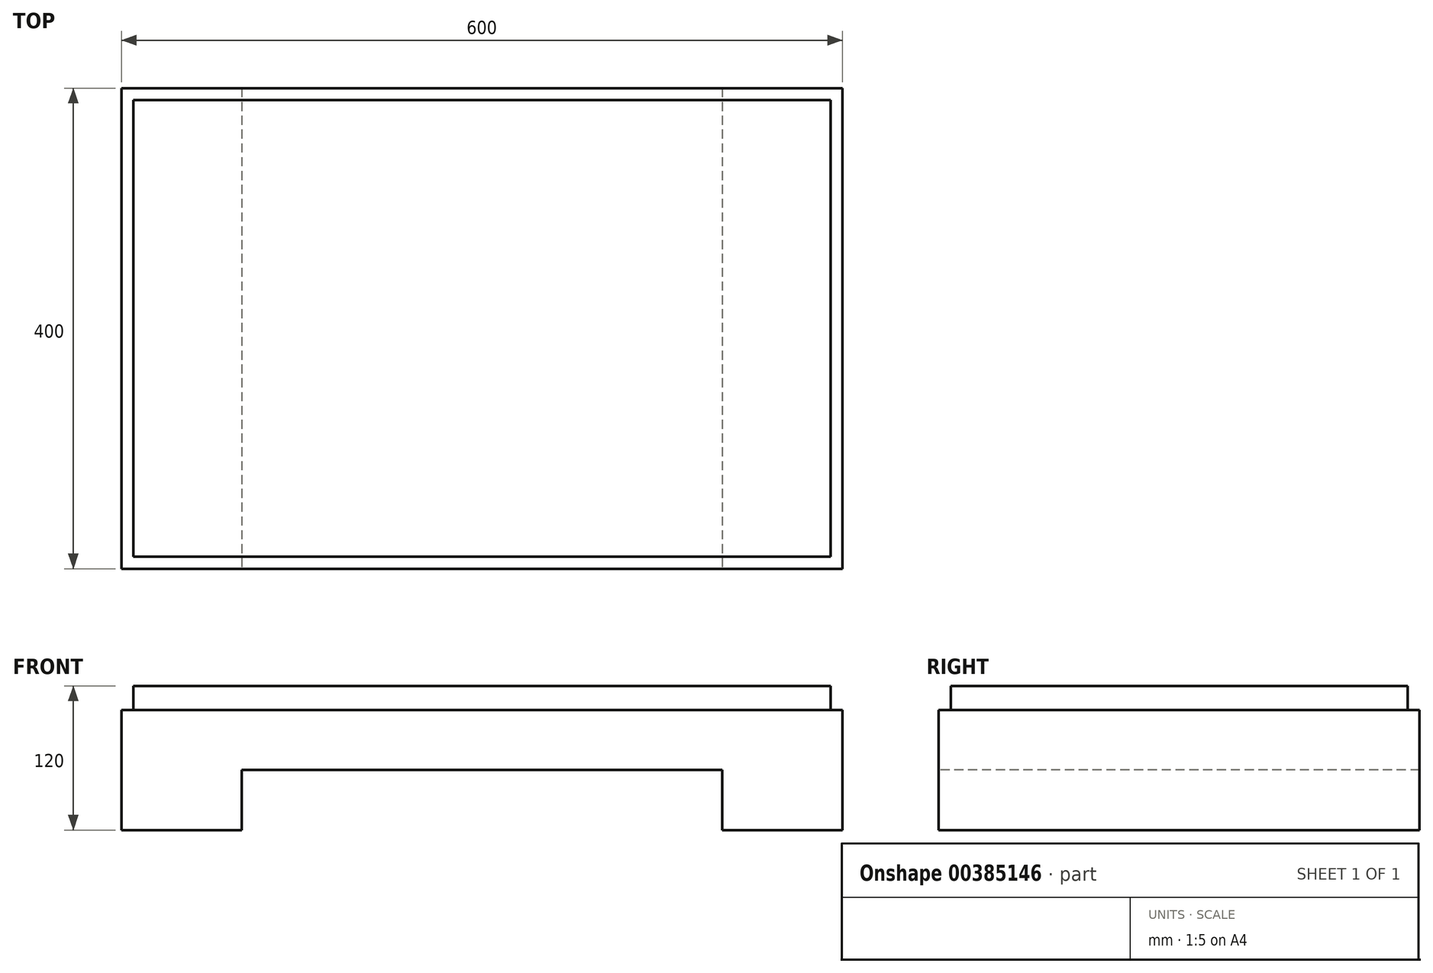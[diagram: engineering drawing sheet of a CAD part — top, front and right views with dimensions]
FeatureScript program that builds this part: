
annotation { "Feature Type Name" : "Feature", "Feature Type Description" : "" }
export const myFeature = defineFeature(function(context is Context, id is Id, definition is map)
    precondition{}
    {
        {
            var Q0;
            Q0=qCreatedBy(makeId("Top.planeOp"),FACE);
            var sketch = newSketch(context, id + "F0", { "sketchPlane" : qUnion([Q0])});
            skLineSegment(sketch, "E0.bottom", {"start": v(-300, 200) * mm, "end": v(300, 200) * mm});
            skLineSegment(sketch, "E0.top", {"start": v(-300, -200) * mm, "end": v(300, -200) * mm});
            skLineSegment(sketch, "E0.left", {"start": v(-300, 200) * mm, "end": v(-300, -200) * mm});
            skLineSegment(sketch, "E0.right", {"start": v(300, 200) * mm, "end": v(300, -200) * mm});
            skPoint(sketch, "E0.middle", {"position": v(0, 0) * mm});
            skSolve(sketch);
        }
        {
            var Q0;
            Q0=makeQuery(id+"F0.imprint","IMPRINT",FACE,{"disambiguationData":[TD([[makeQuery(id+"F0.imprint","IMPRINT",EDGE,{"derivedFrom":sQuery(id+"F0.wireOp",EDGE,"E0.bottom")}),-1.0]])]});
            extrude(context, id + "F1", {"entities" : qUnion([Q0]), "oppositeDirection" : true, "depth" : 100 * mm});
        }
        {
            var Q0;
            Q0=makeQuery(id+"F1.opExtrude","CAP_FACE",FACE,{"disambiguationData":[OSD([sQuery(id+"F0.wireOp",EDGE,"E0.bottom"),sQuery(id+"F0.wireOp",EDGE,"E0.top"),sQuery(id+"F0.wireOp",EDGE,"E0.left"),sQuery(id+"F0.wireOp",EDGE,"E0.right")])],"isStart":false});
            var sketch = newSketch(context, id + "F2", { "sketchPlane" : qUnion([Q0])});
            skLineSegment(sketch, "E1.bottom", {"start": v(-290, 190) * mm, "end": v(290, 190) * mm});
            skLineSegment(sketch, "E1.top", {"start": v(-290, -190) * mm, "end": v(290, -190) * mm});
            skLineSegment(sketch, "E1.left", {"start": v(-290, 190) * mm, "end": v(-290, -190) * mm});
            skLineSegment(sketch, "E1.right", {"start": v(290, 190) * mm, "end": v(290, -190) * mm});
            skPoint(sketch, "E1.middle", {"position": v(0, 0) * mm});
            skSolve(sketch);
        }
        {
            var Q0;
            Q0=makeQuery(id+"F2.imprint","IMPRINT",FACE,{"disambiguationData":[TD([[makeQuery(id+"F2.imprint","IMPRINT",EDGE,{"derivedFrom":sQuery(id+"F2.wireOp",EDGE,"E1.bottom")}),-1.0]])]});
            extrude(context, id + "F3", {"entities" : qUnion([Q0]), "operationType" : NewBodyOperationType.REMOVE, "oppositeDirection" : true, "depth" : 80 * mm});
        }
        {
            var Q0;
            Q0=makeQuery(id+"F1.opExtrude","SWEPT_FACE",FACE,{"disambiguationData":[OSD([sQuery(id+"F0.wireOp",EDGE,"E0.top")])]});
            var sketch = newSketch(context, id + "F4", { "sketchPlane" : qUnion([Q0])});
            skLineSegment(sketch, "E2", {"start": v(-200, -100) * mm, "end": v(-200, -50) * mm});
            skLineSegment(sketch, "E3", {"start": v(-200, -50) * mm, "end": v(200, -50) * mm});
            skPoint(sketch, "E3.endSnap0", {"position": v(300, -50) * mm});
            skLineSegment(sketch, "E4", {"start": v(200, -50) * mm, "end": v(200, -100) * mm});
            skSolve(sketch);
        }
        {
            var Q0;
            Q0 = qSketchRegion(id + "F4", true);
            var Q1;
            {var subQ0=sQuery(id+"F4.wireOp",EDGE,"E2");Q1=makeQuery(id+"F4.imprint","IMPRINT",FACE,{"disambiguationData":[TD([[makeQuery(id+"F4.imprint","IMPRINT",EDGE,{"derivedFrom":subQ0}),-1.0]])]});}
            extrude(context, id + "F5", {"entities" : qUnion([Q0, Q1]), "operationType" : NewBodyOperationType.REMOVE, "oppositeDirection" : true, "depth" : 25 * mm});
        }
        {
            var Q0;
            Q0=makeQuery(id+"F1.opExtrude","SWEPT_FACE",FACE,{"disambiguationData":[OSD([sQuery(id+"F0.wireOp",EDGE,"E0.bottom")])]});
            var sketch = newSketch(context, id + "F6", { "sketchPlane" : qUnion([Q0])});
            skLineSegment(sketch, "E5", {"start": v(-200, -100) * mm, "end": v(-200, -50) * mm});
            skLineSegment(sketch, "E6", {"start": v(-200, -50) * mm, "end": v(200, -50) * mm});
            skLineSegment(sketch, "E7", {"start": v(200, -50) * mm, "end": v(200, -100) * mm});
            skSolve(sketch);
        }
        {
            var Q0;
            Q0 = qSketchRegion(id + "F6", true);
            var Q1;
            {var subQ0=sQuery(id+"F6.wireOp",EDGE,"E5");Q1=makeQuery(id+"F6.imprint","IMPRINT",FACE,{"disambiguationData":[TD([[makeQuery(id+"F6.imprint","IMPRINT",EDGE,{"derivedFrom":subQ0}),-1.0]])]});}
            extrude(context, id + "F7", {"entities" : qUnion([Q0, Q1]), "operationType" : NewBodyOperationType.REMOVE, "oppositeDirection" : true, "depth" : 25 * mm});
        }
        {
            var Q0;
            Q0=makeQuery(id+"F1.opExtrude","CAP_FACE",FACE,{"disambiguationData":[OSD([sQuery(id+"F0.wireOp",EDGE,"E0.bottom"),sQuery(id+"F0.wireOp",EDGE,"E0.top"),sQuery(id+"F0.wireOp",EDGE,"E0.left"),sQuery(id+"F0.wireOp",EDGE,"E0.right")])],"isStart":true});
            var sketch = newSketch(context, id + "F8", { "sketchPlane" : qUnion([Q0])});
            skLineSegment(sketch, "E8.bottom", {"start": v(290, -190) * mm, "end": v(-290, -190) * mm});
            skLineSegment(sketch, "E8.top", {"start": v(290, 190) * mm, "end": v(-290, 190) * mm});
            skLineSegment(sketch, "E8.left", {"start": v(290, -190) * mm, "end": v(290, 190) * mm});
            skLineSegment(sketch, "E8.right", {"start": v(-290, -190) * mm, "end": v(-290, 190) * mm});
            skPoint(sketch, "E8.middle", {"position": v(0, 0) * mm});
            skSolve(sketch);
        }
        {
            var Q0;
            Q0=makeQuery(id+"F8.imprint","IMPRINT",FACE,{"disambiguationData":[TD([[makeQuery(id+"F8.imprint","IMPRINT",EDGE,{"derivedFrom":sQuery(id+"F8.wireOp",EDGE,"E8.bottom")}),-1.0]])]});
            extrude(context, id + "F9", {"entities" : qUnion([Q0]), "operationType" : NewBodyOperationType.ADD, "depth" : 20 * mm});
        }
        {
            var Q0;
            Q0 = qSketchRegion(id + "F4", true);
            var Q1;
            Q1=makeQuery(id+"F1.opExtrude","SWEPT_FACE",FACE,{"disambiguationData":[OSD([sQuery(id+"F0.wireOp",EDGE,"E0.top")])]});
            extrude(context, id + "F10", {"entities" : qUnion([Q0, Q1]), "operationType" : NewBodyOperationType.ADD, "oppositeDirection" : true, "depth" : 400 * mm});
        }
    });
